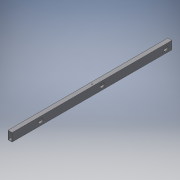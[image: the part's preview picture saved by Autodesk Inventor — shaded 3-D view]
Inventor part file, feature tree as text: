
AUTODESK INVENTOR PART (.ipt)
format: ipt  version: 2018.3 (Build 223284000, 284)  size: 196,608 bytes
history: native  units: in
note: dims shown in document units (in); Inventor stores cm internally (conversion verified against a paired STEP export)
features: extrude x9, sketch x9
ambient origin geometry x8: Origin, YZ Plane, XZ Plane, XY Plane, X Axis, Y Axis, Z Axis, Center Point
bodies: Solid1 (feature_tree)
feature tree (18):
  extrude  "Extrusion1"  Depth=2.0in
  extrude  "Extrusion2"  Depth=0.125in TaperAngle=0.0deg
  extrude  "Extrusion3"  Depth=0.5in TaperAngle=0.0deg
  extrude  "Extrusion4"  Depth=1.0in
  extrude  "Extrusion5"  Depth=1.0in TaperAngle=0.0deg
  extrude  "Extrusion7"  Depth=1.125in
  extrude  "Extrusion9"  Depth=1.0in
  extrude  "Extrusion10"  Depth=1.0in
  extrude  "Extrusion11"  Depth=0.5in
  sketch  "Sketch1"  dims[d0=1.0in d1=2.0in]
  sketch  "Sketch2"  dims[d2=0.125in d3=38.5in d4=0.0in]
  sketch  "Sketch3"  dims[d5=1.0in d7=0.5in d8=0.0in]
  sketch  "Sketch4"  dims[d9=1.0in d10=7.0in]
  sketch  "Sketch5"  dims[d11=1.125in d12=1.0in d13=0.0in]
  sketch  "Sketch7"  dims[d14=22.0in d15=1.125in]
  sketch  "Sketch8"  dims[d16=1.0in d17=0.0in d18=1.0in]
  sketch  "Sketch9"  dims[d19=135.0deg d20=1.0in]
  sketch  "Sketch10"  dims[d21=0.16in d22=0.16in d23=1.0in d24=0.0in d34=1.0in d35=1.125in d36=0.5in d37=0.0in d45=0.9375in d46=0.2031in d47=0.2031in d48=0.2031in d49=0.2031in d50=1.0in d51=0.0in d52=0.125in d53=2.0in d54=1.0in d55=0.125in d56=0.125in d57=2.0in d58=1.0in d59=0.125in d60=0.5in d61=0.0in d62=20.0in d63=90.0deg d64=0.2031in d65=4.0in d66=0.0in]
